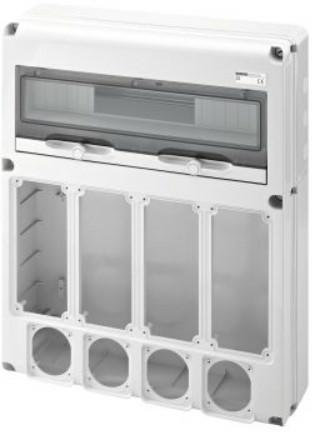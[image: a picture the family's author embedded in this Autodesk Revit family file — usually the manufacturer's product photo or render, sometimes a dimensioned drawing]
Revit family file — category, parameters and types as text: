
# Revit family: Building-QuadriIEC309-GEWISS-68QDIN-QUADRI-PRESE-20MOD_4PRESE_IB_VERT_4PRESE
name_source: partatom
category: Apparecchi elettrici
units: mm (PartAtom-declared; Revit-internal decimal feet)

## family parameters
Condiviso = No
Host = Superficie
Mantenere orientamento annotazione = Sì
Punto di calcolo locali = Sì
Quota connettore circolare = Usa diametro
Taglio con vuoti quando caricato = No
Tipo di parte = Normale

## types (1)
- GW68015N - Q-DIN 20M 4FL.PR.BL.VR.SBF 4FL.16A IP65
    Catalogo = BUILDING
    Catalogo Serie = 68 QDIN
    Classe isolamento = II
    Codice EAN = 8011564744844
    Codice Electrocod = 2242
    Colore = Grigio RAL 7035
    Conformità normativa = EN 60208 - EN 60670-1 - IEC 60670-24
    Descrizione = Q-DIN 20M 4FL.PR.BL.VR.SBF 4FL.16A IP65
    Glow Wire Test = 650°C
    Grado di protezione = IP65
    IDF = 41e3edcd-76e9-4373-aeca-4c72d33b4e2e
    IDT = 5bb38b2c-aa49-47b5-9d7c-4db2ea1b42ab
    Immagine tipo = GW68015N.jpg
    L_Moduli = 380 mm  [stored 1.24672 ft]
    Modello = GW68015N
    N. coperchi ciechi in dotazione = 2 IB 16/32A + 4 IEC 16 A
    N. flange in dotazione = 2 IB 16/32A + 4 IEC 16 A
    N. mod. EN 50022 = 20
    N. prese IB alloggiabili: = 4 IB 16/32 A IP67 + 4 IEC MAX 3P+T 16 A
    N. prese alloggiabili = 4 IB 16/32 A IP67 + 4 IEC MAX 3P+T 16 A
    N_Moduli = 20 mm  [stored 0.0656168 ft]
    POMELLO = bianco
    PRESA = rosso
    Potenza dissipabile A (W) = 30
    Potenza dissipabile B (W) = 92
    Produttore = GEWISS S.p.A.
    Prospetto di default = 1219 mm
    Resistenza agli urti = IK08
    SEO = Quadretto
    STRUTTURA = RAL - 7035
    STRUTTURA ALTA = Poche
    Scheda Tecnica = https://www.gewiss.com
    Spostamento_S = 1000 mm  [stored 3.28084 ft]
    Temperatura di funzionamento = -25 ÷ +40 °C
    Temperatura di utilizzo = -25 +40 °C
    Termopressione con biglia = 70 °C
    Tipo versione = Vuoto
    Tipologia di installazione = Da parete
    URL = https://www.gewiss.com
    VETRO = Vetro
    Versione file RFA = 21.5

note: [stored X ft] marks values corroborated as IEEE doubles in the binary element streams (Revit-internal decimal feet)

## geometry (parser evidence)
native form markers: Sweep x4
no freeform markers — native parametric forms only
